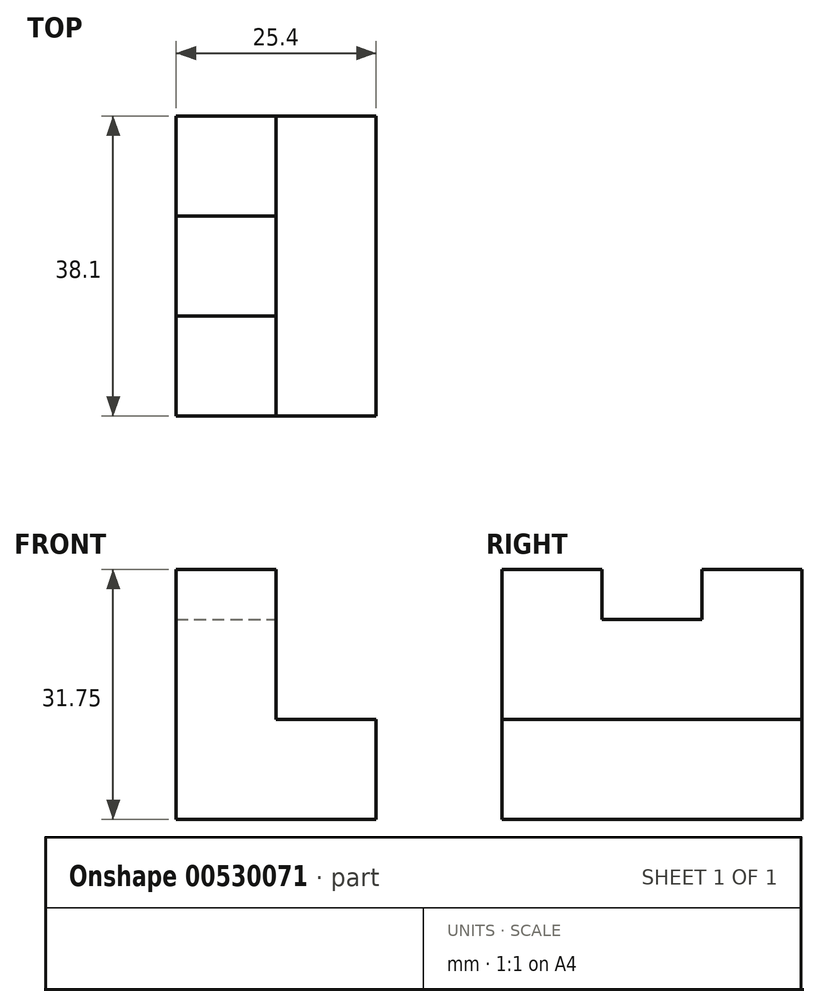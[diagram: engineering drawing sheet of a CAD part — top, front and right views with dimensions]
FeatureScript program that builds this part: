
annotation { "Feature Type Name" : "Feature", "Feature Type Description" : "" }
export const myFeature = defineFeature(function(context is Context, id is Id, definition is map)
    precondition{}
    {
        {
            var Q0;
            Q0=qCreatedBy(makeId("Front.planeOp"),FACE);
            var sketch = newSketch(context, id + "F0", { "sketchPlane" : qUnion([Q0])});
            skLineSegment(sketch, "E0", {"start": v(-55.74, 49.64) * mm, "end": v(-55.74, 17.9) * mm});
            skLineSegment(sketch, "E1", {"start": v(-55.74, 17.9) * mm, "end": v(-30.34, 17.9) * mm});
            skLineSegment(sketch, "E2", {"start": v(-30.34, 17.9) * mm, "end": v(-30.34, 30.6) * mm});
            skLineSegment(sketch, "E3", {"start": v(-30.34, 30.6) * mm, "end": v(-43.04, 30.6) * mm});
            skLineSegment(sketch, "E4", {"start": v(-43.04, 30.6) * mm, "end": v(-43.04, 49.64) * mm});
            skLineSegment(sketch, "E5", {"start": v(-43.04, 49.64) * mm, "end": v(-55.74, 49.64) * mm});
            skSolve(sketch);
        }
        {
            var Q0;
            Q0=makeQuery(id+"F0.imprint","IMPRINT",FACE,{"disambiguationData":[TD([[makeQuery(id+"F0.imprint","IMPRINT",EDGE,{"derivedFrom":sQuery(id+"F0.wireOp",EDGE,"E0")}),1.0]])]});
            extrude(context, id + "F1", {"entities" : qUnion([Q0]), "depth" : 38.1 * mm, "offsetDistance" : 25.4 * mm});
        }
        {
            var Q0;
            Q0=makeQuery(id+"F1.opExtrude","SWEPT_FACE",FACE,{"disambiguationData":[OSD([sQuery(id+"F0.wireOp",EDGE,"E4")])]});
            var sketch = newSketch(context, id + "F2", { "sketchPlane" : qUnion([Q0])});
            skLineSegment(sketch, "E6", {"start": v(-24.07, 49.64) * mm, "end": v(-24.07, 43.3) * mm});
            skLineSegment(sketch, "E7", {"start": v(-24.07, 43.3) * mm, "end": v(-11.37, 43.3) * mm});
            skLineSegment(sketch, "E8", {"start": v(-11.37, 43.3) * mm, "end": v(-11.37, 49.64) * mm});
            skSolve(sketch);
        }
        {
            var Q0;
            {var subQ0=sQuery(id+"F2.wireOp",EDGE,"E6");Q0=makeQuery(id+"F2.imprint","IMPRINT",FACE,{"disambiguationData":[TD([[makeQuery(id+"F2.imprint","IMPRINT",EDGE,{"derivedFrom":subQ0}),1.0]])]});}
            extrude(context, id + "F3", {"entities" : qUnion([Q0]), "operationType" : NewBodyOperationType.ADD, "depth" : 12.7 * mm, "offsetDistance" : 25.4 * mm});
        }
        {
            var Q0;
            Q0=makeQuery(id+"F3.opExtrude","CAP_FACE",FACE,{"disambiguationData":[OSD([sQuery(id+"F0.wireOp",EDGE,"E4"),sQuery(id+"F0.wireOp",EDGE,"E5"),sQuery(id+"F2.wireOp",EDGE,"E6"),sQuery(id+"F2.wireOp",EDGE,"E7"),sQuery(id+"F2.wireOp",EDGE,"E8")])],"isStart":false});
            extrude(context, id + "F4", {"entities" : qUnion([Q0]), "operationType" : NewBodyOperationType.REMOVE, "oppositeDirection" : true, "depth" : 12.7 * mm, "offsetDistance" : 25.4 * mm});
        }
        {
            var Q0;
            {var subQ0=sQuery(id+"F0.wireOp",EDGE,"E4");Q0=makeQuery(id+"F4.boolean.opBoolean","MERGE",FACE,{"derivedFrom":[makeQuery(id+"F1.opExtrude","SWEPT_FACE",FACE,{"disambiguationData":[OSD([subQ0])]}),makeQuery(id+"F4.opExtrude","CAP_FACE",FACE,{"disambiguationData":[OSD([subQ0,sQuery(id+"F0.wireOp",EDGE,"E5"),sQuery(id+"F2.wireOp",EDGE,"E6"),sQuery(id+"F2.wireOp",EDGE,"E7"),sQuery(id+"F2.wireOp",EDGE,"E8")])],"isStart":false})]});}
            var sketch = newSketch(context, id + "F5", { "sketchPlane" : qUnion([Q0])});
            skLineSegment(sketch, "E9", {"start": v(-25.4, 49.64) * mm, "end": v(-25.4, 43.3) * mm});
            skLineSegment(sketch, "E10", {"start": v(-25.4, 43.3) * mm, "end": v(-12.7, 43.3) * mm});
            skLineSegment(sketch, "E11", {"start": v(-12.7, 43.3) * mm, "end": v(-12.7, 49.64) * mm});
            skSolve(sketch);
        }
        {
            var Q0;
            {var subQ0=sQuery(id+"F5.wireOp",EDGE,"E9");Q0=makeQuery(id+"F5.imprint","IMPRINT",FACE,{"disambiguationData":[TD([[makeQuery(id+"F5.imprint","IMPRINT",EDGE,{"derivedFrom":subQ0}),1.0]])]});}
            extrude(context, id + "F6", {"entities" : qUnion([Q0]), "operationType" : NewBodyOperationType.REMOVE, "oppositeDirection" : true, "depth" : 12.7 * mm, "offsetDistance" : 25.4 * mm});
        }
    });
